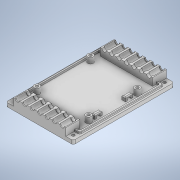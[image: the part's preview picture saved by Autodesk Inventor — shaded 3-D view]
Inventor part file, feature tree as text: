
AUTODESK INVENTOR PART (.ipt)
format: ipt  version: 2021 (Build 250183000, 183)  size: 587,776 bytes
history: native  units: mm
features: extrude x17, sketch x17, fillet x6
ambient origin geometry x8: Origin, YZ Plane, XZ Plane, XY Plane, X Axis, Y Axis, Z Axis, Center Point
bodies: Solid1 (feature_tree)
feature tree (40):
  extrude  "Extrusion1"  Depth=62.0mm
  extrude  "Extrusion2"  Depth=3.0mm
  extrude  "Extrusion3"  Depth=3.0mm
  extrude  "Extrusion4"  Depth=3.0mm
  fillet  "Fillet1"  Radius=6.0mm
  fillet  "Fillet2"  Radius=3.0mm
  fillet  "Fillet3"  Radius=57.4mm
  extrude  "Extrusion7"  Depth=0.8mm
  extrude  "Extrusion8"  Depth=4.8mm
  extrude  "Extrusion9"  Depth=6.0mm
  extrude  "Extrusion10"  Depth=20.0mm
  extrude  "Extrusion11"  Depth=1.0mm
  extrude  "Extrusion12"  Depth=2.0mm TaperAngle=0.0deg
  extrude  "Extrusion13"  TaperAngle=0.0deg  [1 undecoded]
  fillet  "Fillet8"  [1 undecoded]
  fillet  "Fillet9"  Radius=6.0mm
  extrude  "Extrusion14"  TaperAngle=0.0deg  [1 undecoded]
  extrude  "Extrusion15"  Depth=2.0mm
  extrude  "Extrusion16"  Depth=4.0mm
  extrude  "Extrusion17"  Depth=4.0mm
  fillet  "Fillet11"  Radius=2.0mm
  extrude  "Extrusion18"  Depth=2.0mm
  extrude  "Extrusion19"  Depth=35.0mm
  sketch  "Sketch2"  dims[d14=66.0mm d15=62.0mm]
  sketch  "Sketch4"  dims[d16=3.0mm d17=3.0mm]
  sketch  "Sketch5"  dims[d18=3.0mm d19=3.0mm]
  sketch  "Sketch6"  dims[d20=3.0mm d21=4.5mm d22=6.0mm d23=3.0mm d24=57.4mm]
  sketch  "Sketch10"  dims[d25=54.35mm d26=0.8mm]
  sketch  "Sketch11"  dims[d27=51.56mm d28=4.8mm]
  sketch  "Sketch12"  dims[d29=6.0mm d30=6.0mm]
  sketch  "Sketch13"  dims[d31=6.0mm d32=20.0mm]
  sketch  "Sketch14"  dims[d33=20.0mm d34=1.0mm]
  sketch  "Sketch16"  dims[d35=1.0mm d36=2.0mm d37=0.0mm]
  sketch  "Sketch17"  dims[d38=66.0mm d39=62.0mm d40=3.0mm d41=3.0mm d42=3.0mm d43=3.0mm d44=3.0mm d45=4.5mm d46=6.0mm d47=3.0mm d48=57.4mm d49=54.35mm d50=0.8mm d51=51.56mm d52=4.8mm d53=6.0mm d54=6.0mm d55=6.0mm d56=20.0mm d57=20.0mm d58=1.0mm d59=1.0mm d60=0.0mm d61=0.0mm d62=6.0mm d63=0.0mm]
  sketch  "Sketch19"  dims[d64=2.0mm d65=0.0mm]
  sketch  "Sketch20"  dims[d66=2.0mm d67=2.0mm]
  sketch  "Sketch21"  dims[d68=30.0mm d69=4.0mm]
  sketch  "Sketch22"  dims[d70=4.0mm d71=4.0mm d72=2.0mm]
  sketch  "Sketch23"  dims[d73=2.0mm d74=2.0mm]
  sketch  "Sketch24"  dims[d75=2.0mm d76=35.0mm d77=8.0mm d78=0.0mm d79=4.0mm d80=0.0mm d81=1.0mm d82=1.0mm d83=1.0mm d122=15.0mm d123=15.0mm d124=56.0mm d125=4.0mm d126=12.0mm d127=56.0mm d128=4.0mm d129=12.0mm d130=8.0mm d131=0.0mm d132=6.0mm d133=4.0mm d134=70.0mm d136=8.0mm d137=10.0mm d139=10.0mm d141=11.0mm d142=0.0mm d143=6.0mm d144=4.0mm d145=70.0mm d147=8.0mm d148=10.0mm d150=10.0mm d152=11.0mm d153=0.0mm d158=1.0mm d159=1.0mm d160=8.0mm d161=2.0mm d162=0.0mm d163=0.0mm d164=0.0mm d165=4.0mm d166=4.0mm d167=0.0mm d168=2.0mm d169=0.0mm d177=2.0mm d178=2.0mm d179=8.0mm d180=0.0mm d181=2.0mm d182=2.0mm d184=2.0mm d186=2.0mm d187=8.0mm d190=8.0mm d193=8.0mm d196=8.0mm d199=2.0mm d200=2.0mm d201=2.0mm d202=2.0mm d203=2.0mm d204=0.0mm d205=0.5mm d206=0.5mm d211=10.0mm d212=0.0mm d213=2.0mm d214=0.0mm d215=8.0mm d216=5.0mm d217=5.0mm d218=3.0mm d219=8.0mm d220=8.0mm d221=8.0mm d222=5.0mm d223=5.0mm d224=5.0mm d225=5.0mm d226=3.0mm d227=3.0mm d228=3.0mm d229=10.0mm d230=0.0mm d231=7.0mm d232=7.0mm d233=7.0mm d234=7.0mm d235=2.0mm d236=0.0mm d237=2.0mm d238=4.5mm d239=4.0mm d240=70.0mm d242=8.0mm d243=10.0mm d245=10.0mm d247=20.0mm d248=0.0mm d249=4.0mm d250=4.5mm d251=70.0mm d253=8.0mm d254=10.0mm d256=10.0mm d258=20.0mm d259=0.0mm d260=5.0mm d261=5.0mm]
note: 3 required parameter values undecoded (feature->parameter linkage not recoverable at this tier; creation-order binding heuristic only, values carry confidence <= 0.55)
